# Revit family: Sanitary_Wash-basins_DURAVIT-AG_D-Neo-Washbowl-237260
name_source: partatom
category: Plumbing Fixtures
revit_build: Autodesk Revit 2018 (Build: 20190510_1515(x64)
units: mm (PartAtom-declared; Revit-internal decimal feet)

## family parameters
Always vertical = No
Cut with Voids When Loaded = No
OmniClass Number = 23.31.13.00
OmniClass Title = Sinks
Part Type = Normal
Room Calculation Point = No
Round Connector Dimension = Use Diameter
Shared = No
Work Plane-Based = Yes

## types (2) — shared parameters
BIMobject category = Wash basins
Connector Description = Water outlet
Date of publishing = 14.05.2021 00:00:00
Default Elevation = 1219.2 mm  [stored 4 ft]
Details material = Duravit - Metal - 10 - Chrome
EAN code = 4063382136022
ETIM classification = EC011550 | Washbasin
Edition number = 1
IFC Classification = Sanitary Terminal
Installation instructions = http://pro.duravit.com
Manufacturer = Duravit
Manufacturer name = DURAVIT AG
Masterformat 2014 Code = 22 41 16.13
Masterformat 2014 Description = Residential Lavatories
Material main = Ceramics
Model = D-Neo Washbowl - 237260
OmniClass Code = 23-31 13 00
OmniClass Description = Sinks
Outlet Diameter = 32 mm
Product Guid = a81de405-b821-4167-b1a3-a125fa9cd0e6
Product SKU = d-neo-washbowl-237260
Product certification = http://pro.duravit.com
Product data url = https://bimobject.com
Product family = D-Neo
Product group = Washbowl
Product name = D-Neo Washbowl - 237260
Product url = http://pro.duravit.com
QR code = https://bimobject.com
Technical description = http://pro.duravit.com
UNSPSC Code = 30181504
URL = https://www.duravit.com
Uniclass 2015 Code = Pr_40_20_96
Uniclass 2015 Name = Wash basins, sinks and troughs
Uniformat II Code = D2010
Uniformat II Description = Plumbing Fixtures
Weight Net (Kg) = 10,3
Youtube clip = http://pro.duravit.com

## per-type parameters (varying)
| type | Description | Main material |
| 00 - White Alpin | Duravit D-Neo Washbowl 600 mm White High Gloss, Number of faucet holes per wash area: 0 - 2372600070 | Duravit - Ceramic - 00 - White Alpin |
| 00 - White Alpin WonderGliss | Duravit D-Neo Washbowl 600 mm White High Gloss, Number of faucet holes per wash area: 0, WonderGliss - 23726000701 | Duravit - Ceramic - 00 - White Alpin WonderGliss |

note: [stored X ft] marks values corroborated as IEEE doubles in the binary element streams (Revit-internal decimal feet)

## geometry (parser evidence)
native form markers: Sweep x4
no freeform markers — native parametric forms only
